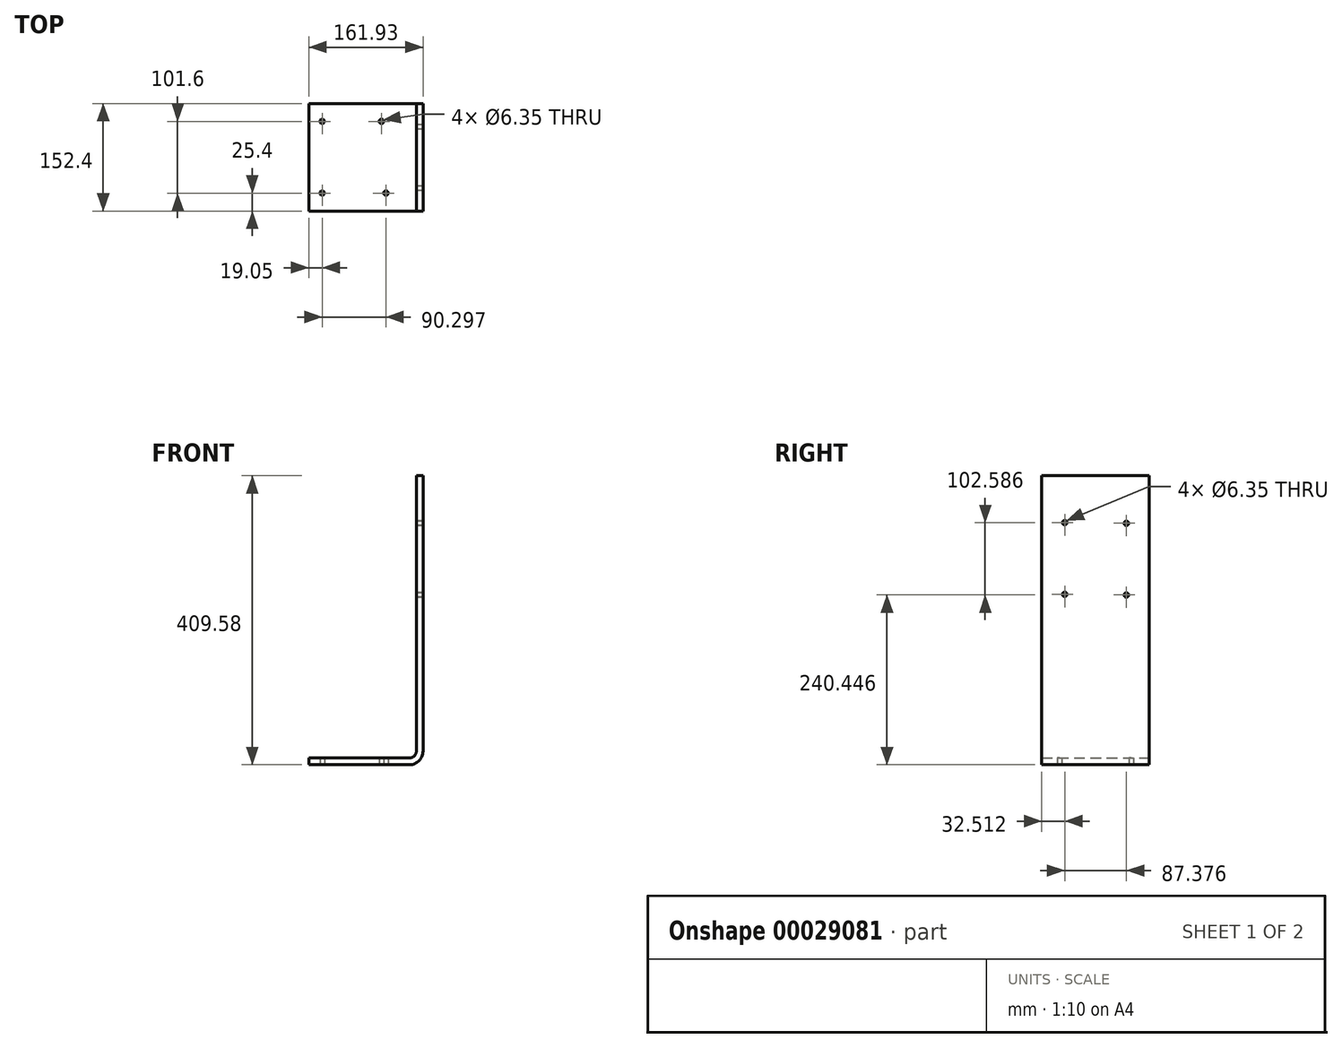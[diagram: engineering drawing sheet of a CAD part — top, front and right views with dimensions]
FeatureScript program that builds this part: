
annotation { "Feature Type Name" : "Feature", "Feature Type Description" : "" }
export const myFeature = defineFeature(function(context is Context, id is Id, definition is map)
    precondition{}
    {
        {
            var Q0;
            Q0=qCreatedBy(makeId("Front.planeOp"),FACE);
            var sketch = newSketch(context, id + "F0", { "sketchPlane" : qUnion([Q0])});
            skLineSegment(sketch, "E0", {"start": v(-152.4, 0) * mm, "end": v(-9.53, 0) * mm});
            skLineSegment(sketch, "E1", {"start": v(0, 9.53) * mm, "end": v(0, 400.05) * mm});
            skLineSegment(sketch, "E2.0", {"start": v(9.53, 9.53) * mm, "end": v(9.53, 400.05) * mm});
            skLineSegment(sketch, "E3.0", {"start": v(-152.4, -9.52) * mm, "end": v(-9.53, -9.52) * mm});
            skLineSegment(sketch, "E4", {"start": v(0, 400.05) * mm, "end": v(9.53, 400.05) * mm});
            skLineSegment(sketch, "E5", {"start": v(-152.4, 0) * mm, "end": v(-152.4, -9.52) * mm});
            skPoint(sketch, "E6.visualSharp", {"position": v(0, 0) * mm});
            skArc(sketch, "E6.filletArc", {"start": v(-9.53, 0) * mm, "mid": v(-2.79, 2.79) * mm, "end": v(0, 9.53) * mm});
            skArc(sketch, "E7.filletArc", {"start": v(-9.53, -9.53) * mm, "mid": v(3.95, -3.95) * mm, "end": v(9.52, 9.53) * mm});
            skSolve(sketch);
        }
        {
            var Q0;
            Q0=makeQuery(id+"F0.imprint","IMPRINT",FACE,{"disambiguationData":[TD([[makeQuery(id+"F0.imprint","IMPRINT",EDGE,{"derivedFrom":sQuery(id+"F0.wireOp",EDGE,"E0")}),-1.0]])]});
            extrude(context, id + "F1", {"entities" : qUnion([Q0]), "depth" : 152.4 * mm});
        }
        {
            var Q0;
            Q0=makeQuery(id+"F1.opExtrude","SWEPT_FACE",FACE,{"disambiguationData":[OSD([sQuery(id+"F0.wireOp",EDGE,"E3.0")])]});
            var sketch = newSketch(context, id + "F2", { "sketchPlane" : qUnion([Q0])});
            skCircle(sketch, "E8", {"center": v(-133.35, 25.4) * mm, "radius": 3.18 * mm});
            skLineSegment(sketch, "E9", {"start": v(-152.4, 76.2) * mm, "end": v(28.2, 76.2) * mm, "construction": true});
            skSolve(sketch);
        }
        {
            var Q0;
            Q0=makeQuery(id+"F2.imprint","IMPRINT",FACE,{"disambiguationData":[TD([[makeQuery(id+"F2.imprint","IMPRINT",EDGE,{"derivedFrom":sQuery(id+"F2.wireOp",EDGE,"E8")}),1.0]])]});
            extrude(context, id + "F3", {"entities" : qUnion([Q0]), "operationType" : NewBodyOperationType.REMOVE, "endBound" : BoundingType.THROUGH_ALL, "oppositeDirection" : true, "depth" : 25.4 * mm});
        }
        {
            var Q0;
            Q0=qCreatedBy(makeId("Front.planeOp"),FACE);
            cPlane(context, id + "F4", {"entities" : qUnion([Q0]), "cplaneType" : CPlaneType.OFFSET, "offset" : 76.2 * mm, "width" : 152.4 * mm, "height" : 152.4 * mm});
        }
        {
            var Q0;
            Q0=makeQuery(id+"F3.boolean.opBoolean","COPY",FACE,{"derivedFrom":makeQuery(id+"F3.opExtrude","SWEPT_FACE",FACE,{"disambiguationData":[OSD([sQuery(id+"F2.wireOp",EDGE,"E8")])]})});
            var Q1;
            Q1=qCreatedBy(id+"F4.planeOp",FACE);
            mirror(context, id + "F5", {"operationType" : NewBodyOperationType.REMOVE, "faces" : qUnion([Q0]), "mirrorPlane" : qUnion([Q1]), "patternType" : MirrorType.FACE});
        }
        {
            var Q0;
            Q0=makeQuery(id+"F1.opExtrude","SWEPT_FACE",FACE,{"disambiguationData":[OSD([sQuery(id+"F0.wireOp",EDGE,"E3.0")])]});
            var sketch = newSketch(context, id + "F6", { "sketchPlane" : qUnion([Q0])});
            skCircle(sketch, "E10", {"center": v(-49.4, 25.4) * mm, "radius": 3.18 * mm});
            skCircle(sketch, "E11", {"center": v(-43.05, 127) * mm, "radius": 3.18 * mm});
            skSolve(sketch);
        }
        {
            var Q0;
            Q0=makeQuery(id+"F6.imprint","IMPRINT",FACE,{"disambiguationData":[TD([[makeQuery(id+"F6.imprint","IMPRINT",EDGE,{"derivedFrom":sQuery(id+"F6.wireOp",EDGE,"E11")}),1.0]])]});
            var Q1;
            Q1=makeQuery(id+"F6.imprint","IMPRINT",FACE,{"disambiguationData":[TD([[makeQuery(id+"F6.imprint","IMPRINT",EDGE,{"derivedFrom":sQuery(id+"F6.wireOp",EDGE,"E10")}),1.0]])]});
            extrude(context, id + "F7", {"entities" : qUnion([Q0, Q1]), "operationType" : NewBodyOperationType.REMOVE, "oppositeDirection" : true, "depth" : 25.4 * mm});
        }
        {
            var Q0;
            Q0=makeQuery(id+"F1.opExtrude","SWEPT_FACE",FACE,{"disambiguationData":[OSD([sQuery(id+"F0.wireOp",EDGE,"E2.0")])]});
            var sketch = newSketch(context, id + "F8", { "sketchPlane" : qUnion([Q0])});
            skCircle(sketch, "E12", {"center": v(-119.89, 231.9) * mm, "radius": 3.18 * mm});
            skCircle(sketch, "E13", {"center": v(-32.51, 230.92) * mm, "radius": 3.18 * mm});
            skCircle(sketch, "E14", {"center": v(-119.89, 333.5) * mm, "radius": 3.18 * mm});
            skCircle(sketch, "E15", {"center": v(-32.52, 332.52) * mm, "radius": 3.18 * mm});
            skSolve(sketch);
        }
        {
            var Q0;
            Q0=makeQuery(id+"F8.imprint","IMPRINT",FACE,{"disambiguationData":[TD([[makeQuery(id+"F8.imprint","IMPRINT",EDGE,{"derivedFrom":sQuery(id+"F8.wireOp",EDGE,"E14")}),1.0]])]});
            var Q1;
            Q1=makeQuery(id+"F8.imprint","IMPRINT",FACE,{"disambiguationData":[TD([[makeQuery(id+"F8.imprint","IMPRINT",EDGE,{"derivedFrom":sQuery(id+"F8.wireOp",EDGE,"E15")}),1.0]])]});
            var Q2;
            Q2=makeQuery(id+"F8.imprint","IMPRINT",FACE,{"disambiguationData":[TD([[makeQuery(id+"F8.imprint","IMPRINT",EDGE,{"derivedFrom":sQuery(id+"F8.wireOp",EDGE,"E13")}),1.0]])]});
            var Q3;
            Q3=makeQuery(id+"F8.imprint","IMPRINT",FACE,{"disambiguationData":[TD([[makeQuery(id+"F8.imprint","IMPRINT",EDGE,{"derivedFrom":sQuery(id+"F8.wireOp",EDGE,"E12")}),1.0]])]});
            extrude(context, id + "F9", {"entities" : qUnion([Q0, Q1, Q2, Q3]), "operationType" : NewBodyOperationType.REMOVE, "oppositeDirection" : true, "depth" : 25.4 * mm});
        }
    });
